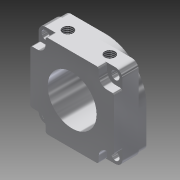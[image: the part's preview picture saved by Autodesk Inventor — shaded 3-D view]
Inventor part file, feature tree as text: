
AUTODESK INVENTOR PART (.ipt)
format: ipt  version: 2014 SP1 (Build 180222100, 222)  size: 279,552 bytes
history: native  units: in
note: dims shown in document units (in); Inventor stores cm internally (conversion verified against a paired STEP export)
features: extrude x6, sketch x4, thread x4, fillet x2
ambient origin geometry x8: Origin, YZ Plane, XZ Plane, XY Plane, X Axis, Y Axis, Z Axis, Center Point
bodies: Solid1 (feature_tree)
feature tree (16):
  sketch  "Sketch1"  dims[d0=1.5in d1=1.5in]
  extrude  "Extrusion1"  Depth=1.5in
  extrude  "Extrusion2"  Depth=0.125in
  fillet  "Fillet1"  Radius=0.125in
  extrude  "Extrusion3"  Depth=0.75in
  extrude  "Extrusion4"  Depth=0.0394in
  thread  "Thread1"  [1 undecoded]
  thread  "Thread2"  [1 undecoded]
  thread  "Thread3"  [1 undecoded]
  thread  "Thread4"  [1 undecoded]
  fillet  "Fillet2"  Radius=0.15in
  sketch  "Sketch4"  dims[d14=0.875in d15=0.5in d16=0.125in d17=0.125in d18=0.075in d22=1.5748in d24=360.0deg d26=0.15in d27=0.0in d28=0.45in d29=0.0in d30=0.125in d32=0.375in d33=0.375in d34=0.185in d35=0.185in d36=0.15in d37=0.0in d39=0.375in d40=0.375in d41=0.185in d42=0.185in d43=0.15in d44=0.0in d45=0.3in d46=0.3in d47=1.0in d48=0.0in d49=1.0in d50=0.0in d51=1.0in d52=0.0in d53=1.0in d54=0.0in d55=0.0394in d56=0.0197in d57=0.1575in d58=0.0in d59=1.45in d60=0.625in d64=0.3937in d65=1.1614in d66=0.0394in d67=0.0in d68=45.0deg]
  extrude  "Extrusion5"  Depth=0.45in TaperAngle=0.0deg
  extrude  "Extrusion6"  Depth=0.125in
  sketch  "Sketch2"  dims[d2=0.148in d3=0.7874in d5=1.25in d6=0.7874in d8=1.25in d11=0.125in]
  sketch  "Sketch3"  dims[d12=0.125in d13=0.75in]
note: 4 required parameter values undecoded (feature->parameter linkage not recoverable at this tier; creation-order binding heuristic only, values carry confidence <= 0.55)
